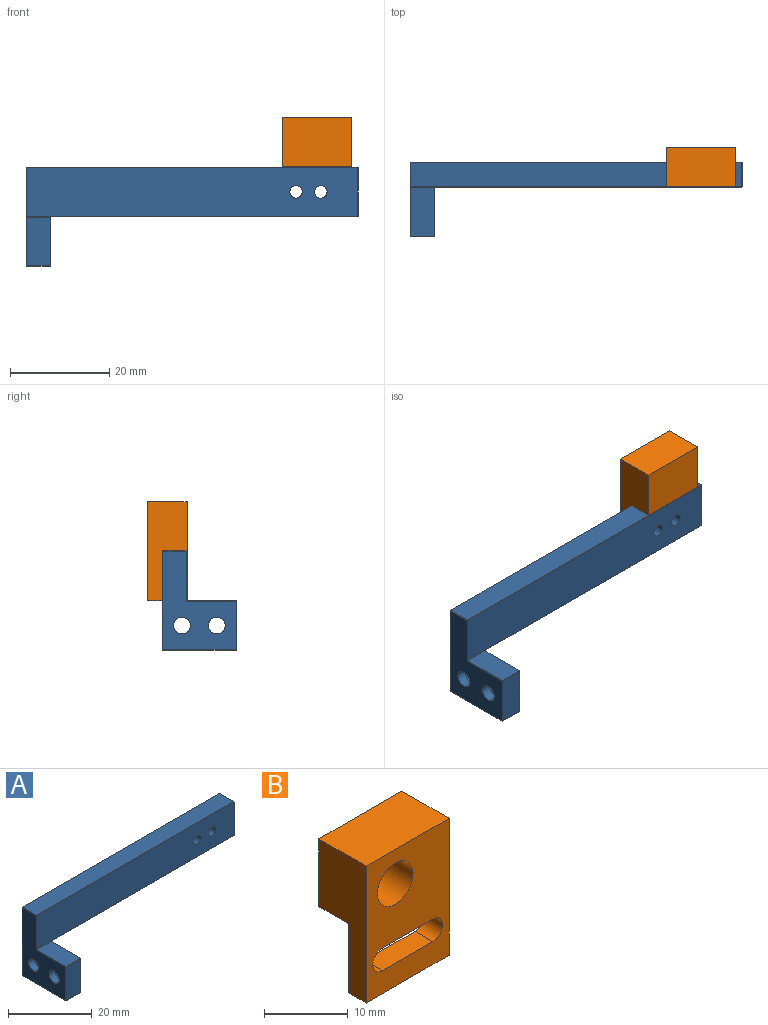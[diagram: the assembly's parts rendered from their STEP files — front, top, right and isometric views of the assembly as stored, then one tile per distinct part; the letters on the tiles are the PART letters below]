
ASSEMBLY  parts=2 mates=1
PART A: 49 faces, bbox 67x15x20 mm
  f0: plane 14.8x10mm, normal (1,0,0), area 80.2mm2, adj f3,f5,f6,f11,f14,f24,f33,f40
  f1: plane 19.8x14.8mm, normal (-1,0,0), area 174.9mm2, adj f9,f12,f18,f22,f25,f26,f29,f30
  f2: plane 66.8x19.8mm, normal (0,1,0), area 692.8mm2, adj f16,f17,f26,f32,f35,f40,f42,f43
  f3: plane 66.8x9.9mm, normal (0,-1,0), area 645.3mm2, adj f0,f6,f16,f17,f29,f37,f44,f45
  f4: plane 66.8x4.8mm, normal (0,0,1), area 320.6mm2, adj f30,f35,f37,f38
  f5: plane 61.9x4.8mm, normal (0,0,-1), area 297.1mm2, adj f0,f43,f44,f48
  f6: plane 9.9x4.9mm, normal (0,0,1), area 48.5mm2, adj f0,f3,f20,f25
  f7: plane 14.8x4.8mm, normal (0,0,-1), area 71mm2, adj f22,f23,f32,f33
  f8: plane 9.8x4.8mm, normal (0,-1,0), area 47mm2, adj f18,f20,f23,f24
  f9: cylinder r=1.7mm len=3.4mm, axis (1,0,0), area 21.4mm2, adj f1,f10
  f10: plane 6.5x6.5mm, normal (1,0,0), area 24.1mm2, adj f9,f11
  f11: cylinder r=3.25mm len=6.5mm, axis (1,0,0), area 61.3mm2, adj f0,f10
  f12: cylinder r=1.7mm len=3.4mm, axis (1,0,0), area 21.4mm2, adj f1,f13
  f13: plane 6.5x6.5mm, normal (1,0,0), area 24.1mm2, adj f12,f14
  f14: cylinder r=3.25mm len=6.5mm, axis (1,0,0), area 61.3mm2, adj f0,f13
  f15: plane 9.8x4.8mm, normal (1,0,0), area 47mm2, adj f38,f42,f45,f48
  f16: cylinder r=1.25mm len=5mm, axis (0,1,0), area 39.3mm2, adj f2,f3
  f17: cylinder r=1.25mm len=5mm, axis (0,1,0), area 39.3mm2, adj f2,f3
  f18: plane 9.8x0.1mm, normal (-0.71,-0.71,0), area 1.4mm2, adj f1,f8,f19,f21
  f19: plane 0.1x0.1mm, normal (-0.58,-0.58,-0.58), area 0mm2, adj f18,f22,f23
  f20: plane 4.9x0.1mm, normal (0,-0.71,0.71), area 0.7mm2, adj f6,f8,f21,f24
  f21: plane 0.1x0.1mm, normal (-0.58,-0.58,0.58), area 0mm2, adj f18,f20,f25
  f22: plane 14.8x0.1mm, normal (-0.71,0,-0.71), area 2.1mm2, adj f1,f7,f19,f27
  f23: plane 4.8x0.1mm, normal (0,-0.71,-0.71), area 0.7mm2, adj f7,f8,f19,f28
  f24: plane 9.9x0.1mm, normal (0.71,-0.71,0), area 1.4mm2, adj f0,f8,f20,f28
  f25: plane 10x0.1mm, normal (-0.71,0,0.71), area 1.4mm2, adj f1,f6,f21,f29
  f26: plane 19.8x0.1mm, normal (-0.71,0.71,0), area 2.8mm2, adj f1,f2,f27,f31
  f27: plane 0.1x0.1mm, normal (-0.58,0.58,-0.58), area 0mm2, adj f22,f26,f32
  f28: plane 0.1x0.1mm, normal (0.58,-0.58,-0.58), area 0mm2, adj f23,f24,f33
  f29: plane 10x0.1mm, normal (-0.71,-0.71,0), area 1.4mm2, adj f1,f3,f25,f34
  f30: plane 4.8x0.1mm, normal (-0.71,0,0.71), area 0.7mm2, adj f1,f4,f31,f34
  f31: plane 0.1x0.1mm, normal (-0.58,0.58,0.58), area 0mm2, adj f26,f30,f35
  f32: plane 4.8x0.1mm, normal (0,0.71,-0.71), area 0.7mm2, adj f2,f7,f27,f36
  f33: plane 14.8x0.1mm, normal (0.71,0,-0.71), area 2.1mm2, adj f0,f7,f28,f36
  f34: plane 0.1x0.1mm, normal (-0.58,-0.58,0.58), area 0mm2, adj f29,f30,f37
  f35: plane 66.8x0.1mm, normal (0,0.71,0.71), area 9.4mm2, adj f2,f4,f31,f39
  f36: plane 0.1x0.1mm, normal (0.58,0.58,-0.58), area 0mm2, adj f32,f33,f40
  f37: plane 66.8x0.1mm, normal (0,-0.71,0.71), area 9.4mm2, adj f3,f4,f34,f41
  f38: plane 4.8x0.1mm, normal (0.71,0,0.71), area 0.7mm2, adj f4,f15,f39,f41
  f39: plane 0.1x0.1mm, normal (0.58,0.58,0.58), area 0mm2, adj f35,f38,f42
  f40: plane 10x0.1mm, normal (0.71,0.71,0), area 1.4mm2, adj f0,f2,f36,f43
  f41: plane 0.1x0.1mm, normal (0.58,-0.58,0.58), area 0mm2, adj f37,f38,f45
  f42: plane 9.8x0.1mm, normal (0.71,0.71,0), area 1.4mm2, adj f2,f15,f39,f46
  f43: plane 62x0.1mm, normal (0,0.71,-0.71), area 8.8mm2, adj f2,f5,f40,f46
  f44: plane 61.9x0.1mm, normal (0,-0.71,-0.71), area 8.8mm2, adj f0,f3,f5,f47
  f45: plane 9.8x0.1mm, normal (0.71,-0.71,0), area 1.4mm2, adj f3,f15,f41,f47
  f46: plane 0.1x0.1mm, normal (0.58,0.58,-0.58), area 0mm2, adj f42,f43,f48
  f47: plane 0.1x0.1mm, normal (0.58,-0.58,-0.58), area 0mm2, adj f44,f45,f48
  f48: plane 4.8x0.1mm, normal (0.71,0,-0.71), area 0.7mm2, adj f5,f15,f46,f47
PART B: 14 faces, bbox 14x8x20 mm
  f0: plane 20x8mm, normal (1,0,0), area 109.5mm2, adj f1,f2,f4,f9,f10,f11
  f1: plane 14x10.1mm, normal (0,1,0), area 104.8mm2, adj f0,f3,f4,f5,f6,f7,f8,f11
  f2: plane 20x14mm, normal (0,-1,0), area 215.1mm2, adj f0,f3,f4,f5,f6,f7,f8,f9
  f3: plane 20x8mm, normal (-1,0,0), area 109.5mm2, adj f1,f2,f4,f9,f10,f11
  f4: plane 14x3mm, normal (0,0,-1), area 42mm2, adj f0,f1,f2,f3
  f5: plane 8.5x3mm, normal (0,0,1), area 25.5mm2, adj f1,f2,f6,f8
  f6: cylinder r=1.65mm len=3.3mm, axis (0,-1,0), area 15.6mm2, adj f1,f2,f5,f7
  f7: plane 8.5x3mm, normal (0,0,-1), area 25.5mm2, adj f1,f2,f6,f8
  f8: cylinder r=1.65mm len=3.3mm, axis (0,-1,0), area 15.6mm2, adj f1,f2,f5,f7
  f9: plane 14x8mm, normal (0,0,1), area 112mm2, adj f0,f2,f3,f10
  f10: plane 14x9.9mm, normal (0,1,0), area 138.6mm2, adj f0,f3,f9,f11
  f11: plane 14x5mm, normal (0,0,-1), area 70mm2, adj f0,f1,f3,f10
  f12: cylinder r=3mm len=7mm, axis (0,-1,0), area 131.9mm2, adj f2,f13
  f13: plane 6x6mm, normal (0,-1,0), area 28.3mm2, adj f12
PLACE A t=(-30.69,-19.51,-5.28)mm
PLACE B rot(axis=(0,0,1),180deg) t=(50.56,12.49,17.72)mm
MATE fastened B.f6 <-> A.f17  axis (0,-1,0) through (21.31,7.49,4.72)mm
